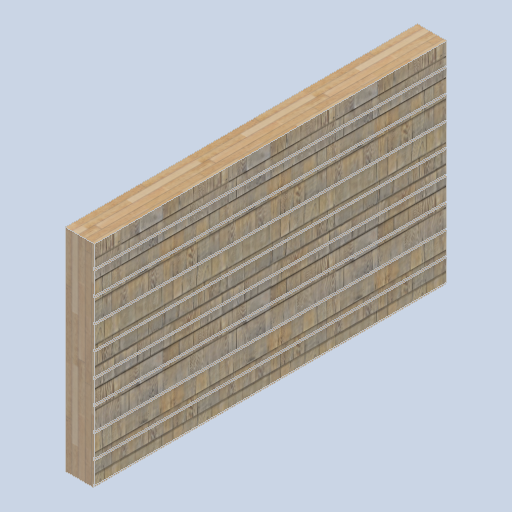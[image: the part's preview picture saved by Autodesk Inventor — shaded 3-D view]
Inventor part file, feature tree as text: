
AUTODESK INVENTOR PART (.ipt)
format: ipt  version: 2024.2 (Build 282272000, 272)  size: 536,064 bytes
history: native  units: mm
features: extrude x2, sketch x2
ambient origin geometry x8: Origin, YZ Plane, XZ Plane, XY Plane, X Axis, Y Axis, Z Axis, Center Point
bodies: Solid1 (feature_tree)
feature tree (4):
  extrude  "Extrusion1"  Depth=180.0mm
  extrude  "Extrusion2"  Depth=180.0mm
  sketch  "Sketch1"  dims[d0=250.0mm d1=0.0mm d2=180.0mm]
  sketch  "Sketch2"  dims[d3=20.0mm d4=180.0mm d5=180.0mm d6=180.0mm d7=180.0mm d8=180.0mm d9=180.0mm d10=180.0mm d11=0.0mm d12=0.0mm]
